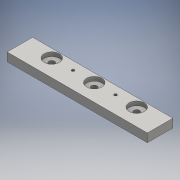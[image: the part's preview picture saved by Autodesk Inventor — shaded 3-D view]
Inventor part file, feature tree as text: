
AUTODESK INVENTOR PART (.ipt)
format: ipt  version: 2016 (Build 200138000, 138)  size: 117,248 bytes
history: native  units: mm
features: sketch x3, hole x2, extrude x1
ambient origin geometry x8: Origin, YZ Plane, XZ Plane, XY Plane, X Axis, Y Axis, Z Axis, Center Point
bodies: Solid1 (feature_tree)
feature tree (6):
  extrude  "Extrusion1"  Depth=30.0mm
  hole  "Hole1"  [1 undecoded]
  hole  "Hole2"  [1 undecoded]
  sketch  "Sketch1"  dims[d0=165.0mm d1=30.0mm]
  sketch  "Sketch2"  dims[d2=82.5mm d3=15.0mm]
  sketch  "Sketch3"  dims[d4=10.0mm d5=0.0mm d6=50.0mm d8=6.6mm d9=6.0mm d10=18.0mm d11=4.8mm d12=90.0deg d13=8.0mm d14=20.594885mm d15=50.0mm d17=3.242mm d18=8.0mm d19=12.6mm d20=2.0mm d21=90.0deg d22=11.8mm d23=20.594885mm d24=50.0mm d25=10.0mm d26=10.0mm d27=25.0mm]
note: 2 required parameter values undecoded (feature->parameter linkage not recoverable at this tier; creation-order binding heuristic only, values carry confidence <= 0.55)
